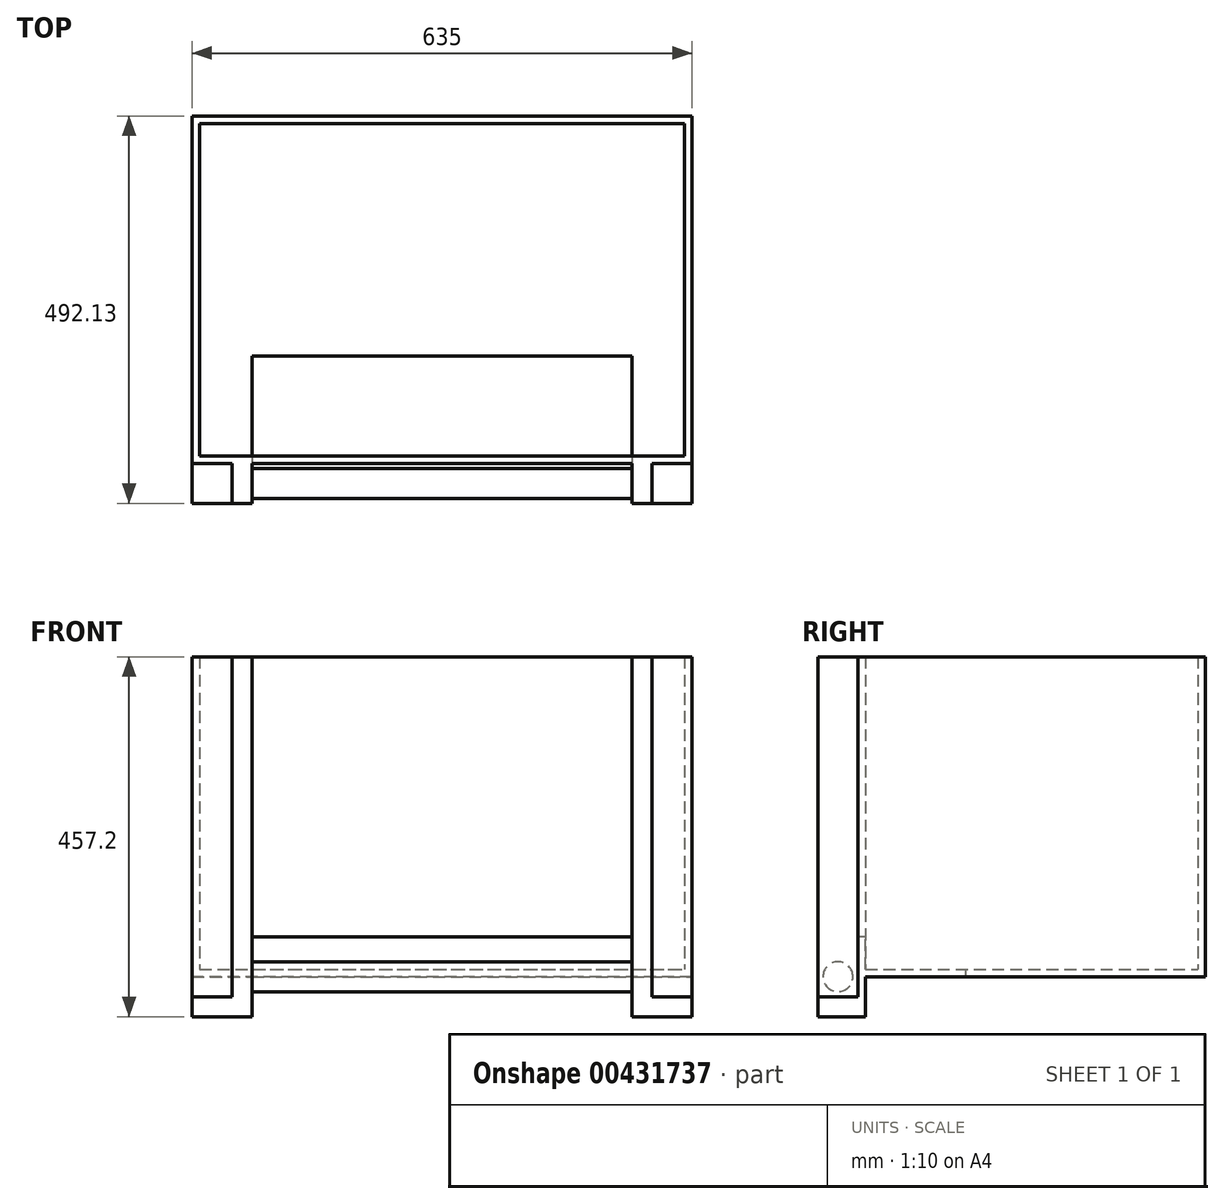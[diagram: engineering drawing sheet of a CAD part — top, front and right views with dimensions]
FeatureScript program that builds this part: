
annotation { "Feature Type Name" : "Feature", "Feature Type Description" : "" }
export const myFeature = defineFeature(function(context is Context, id is Id, definition is map)
    precondition{}
    {
        {
            var Q0;
            Q0=qCreatedBy(makeId("Top.planeOp"),FACE);
            var sketch = newSketch(context, id + "F0", { "sketchPlane" : qUnion([Q0])});
            skLineSegment(sketch, "E0", {"start": v(0, 0) * mm, "end": v(-241.3, 0) * mm, "construction": true});
            skLineSegment(sketch, "E1", {"start": v(-241.3, 0) * mm, "end": v(-241.3, 25.4) * mm, "construction": true});
            skLineSegment(sketch, "E2.bottom", {"start": v(-241.3, 25.4) * mm, "end": v(-266.7, 25.4) * mm});
            skLineSegment(sketch, "E2.top", {"start": v(-241.3, -25.4) * mm, "end": v(-266.7, -25.4) * mm});
            skLineSegment(sketch, "E2.left", {"start": v(-241.3, 25.4) * mm, "end": v(-241.3, -25.4) * mm});
            skLineSegment(sketch, "E2.right", {"start": v(-266.7, 25.4) * mm, "end": v(-266.7, -25.4) * mm});
            skSolve(sketch);
        }
        {
            var Q0;
            Q0=makeQuery(id+"F0.imprint","IMPRINT",FACE,{"disambiguationData":[TD([[makeQuery(id+"F0.imprint","IMPRINT",EDGE,{"derivedFrom":sQuery(id+"F0.wireOp",EDGE,"E2.bottom")}),1.0]])]});
            var Q1;
            Q1=makeQuery(id+"F0.imprint","IMPRINT",FACE,{"disambiguationData":[TD([[makeQuery(id+"F0.imprint","IMPRINT",EDGE,{"derivedFrom":sQuery(id+"F0.wireOp",EDGE,"9ac1ece2-4fc4-431e-a1f0-98b5578401bd1.MirrorCS")}),-1.0]])]});
            extrude(context, id + "F1", {"entities" : qUnion([Q0, Q1]), "depth" : 457.2 * mm});
        }
        {
            var Q0;
            Q0=makeQuery(id+"F1.opExtrude","SWEPT_FACE",FACE,{"disambiguationData":[OSD([sQuery(id+"F0.wireOp",EDGE,"E2.right")])]});
            var sketch = newSketch(context, id + "F2", { "sketchPlane" : qUnion([Q0])});
            skLineSegment(sketch, "E3.bottom", {"start": v(-25.4, 0) * mm, "end": v(25.4, 0) * mm});
            skLineSegment(sketch, "E3.top", {"start": v(-25.4, 25.4) * mm, "end": v(25.4, 25.4) * mm});
            skLineSegment(sketch, "E3.left", {"start": v(-25.4, 0) * mm, "end": v(-25.4, 25.4) * mm});
            skLineSegment(sketch, "E3.right", {"start": v(25.4, 0) * mm, "end": v(25.4, 25.4) * mm});
            skSolve(sketch);
        }
        {
            var Q0;
            Q0=makeQuery(id+"F2.imprint","IMPRINT",FACE,{"disambiguationData":[TD([[makeQuery(id+"F2.imprint","IMPRINT",EDGE,{"derivedFrom":sQuery(id+"F2.wireOp",EDGE,"E3.bottom")}),1.0]])]});
            extrude(context, id + "F3", {"entities" : qUnion([Q0]), "operationType" : NewBodyOperationType.ADD, "depth" : 50.8 * mm});
        }
        {
            var Q0;
            Q0=makeQuery(id+"F1.opExtrude","SWEPT_FACE",FACE,{"disambiguationData":[OSD([sQuery(id+"F0.wireOp",EDGE,"E2.left")])]});
            var sketch = newSketch(context, id + "F4", { "sketchPlane" : qUnion([Q0])});
            skLineSegment(sketch, "E4", {"start": v(0, 0) * mm, "end": v(0, 50.8) * mm, "construction": true});
            skCircle(sketch, "E5", {"center": v(0, 50.8) * mm, "radius": 19.05 * mm});
            skSolve(sketch);
        }
        {
            var Q0;
            Q0 = qSketchRegion(id + "F4", true);
            extrude(context, id + "F5", {"entities" : qUnion([Q0]), "operationType" : NewBodyOperationType.ADD, "depth" : 241.3 * mm});
        }
        {
            var Q0;
            Q0=makeQuery(id+"F1.opExtrude","SWEPT_BODY",BODY,{"disambiguationData":[OSD([sQuery(id+"F0.wireOp",EDGE,"E2.bottom"),sQuery(id+"F0.wireOp",EDGE,"E2.top"),sQuery(id+"F0.wireOp",EDGE,"E2.right"),sQuery(id+"F0.wireOp",EDGE,"E2.left")])]});
            var Q1;
            Q1=qCreatedBy(makeId("Right.planeOp"),FACE);
            mirror(context, id + "F6", {"operationType" : NewBodyOperationType.ADD, "entities" : qUnion([Q0]), "mirrorPlane" : qUnion([Q1])});
        }
        {
            var Q0;
            Q0=makeQuery(id+"F3.boolean.opBoolean","MERGE",FACE,{"derivedFrom":[makeQuery(id+"F1.opExtrude","SWEPT_FACE",FACE,{"disambiguationData":[OSD([sQuery(id+"F0.wireOp",EDGE,"E2.bottom")])]}),makeQuery(id+"F3.opExtrude","SWEPT_FACE",FACE,{"disambiguationData":[OSD([sQuery(id+"F2.wireOp",EDGE,"E3.left")])]})]});
            var sketch = newSketch(context, id + "F7", { "sketchPlane" : qUnion([Q0])});
            skLineSegment(sketch, "E6.bottom", {"start": v(317.5, 0) * mm, "end": v(241.3, 0) * mm});
            skLineSegment(sketch, "E6.top", {"start": v(317.5, 457.2) * mm, "end": v(241.3, 457.2) * mm});
            skLineSegment(sketch, "E6.left", {"start": v(317.5, 0) * mm, "end": v(317.5, 457.2) * mm});
            skLineSegment(sketch, "E6.right", {"start": v(241.3, 0) * mm, "end": v(241.3, 457.2) * mm});
            skLineSegment(sketch, "E7.bottom", {"start": v(241.3, 457.2) * mm, "end": v(0, 457.2) * mm});
            skLineSegment(sketch, "E7.top", {"start": v(241.3, 101.6) * mm, "end": v(0, 101.6) * mm});
            skLineSegment(sketch, "E7.left", {"start": v(241.3, 457.2) * mm, "end": v(241.3, 101.6) * mm});
            skLineSegment(sketch, "E7.right", {"start": v(0, 457.2) * mm, "end": v(0, 101.6) * mm, "construction": true});
            skLineSegment(sketch, "E8.MirrorCS", {"start": v(-241.3, 0) * mm, "end": v(-241.3, 457.2) * mm});
            skLineSegment(sketch, "E9.MirrorCS", {"start": v(-241.3, 457.2) * mm, "end": v(-241.3, 101.6) * mm});
            skLineSegment(sketch, "E10.MirrorCS", {"start": v(-317.5, 0) * mm, "end": v(-241.3, 0) * mm});
            skLineSegment(sketch, "E11.MirrorCS", {"start": v(-317.5, 457.2) * mm, "end": v(-241.3, 457.2) * mm});
            skLineSegment(sketch, "E12.MirrorCS", {"start": v(-241.3, 101.6) * mm, "end": v(0, 101.6) * mm});
            skLineSegment(sketch, "E13.MirrorCS", {"start": v(-241.3, 457.2) * mm, "end": v(0, 457.2) * mm});
            skLineSegment(sketch, "E14.MirrorCS", {"start": v(-317.5, 0) * mm, "end": v(-317.5, 457.2) * mm});
            skSolve(sketch);
        }
        {
            var Q0;
            Q0=makeQuery(id+"F7.imprint","IMPRINT",FACE,{"disambiguationData":[TD([[makeQuery(id+"F7.imprint","IMPRINT",EDGE,{"derivedFrom":sQuery(id+"F7.wireOp",EDGE,"E8.MirrorCS")}),1.0]])]});
            var Q1;
            {var subQ1=sQuery(id+"F0.wireOp",EDGE,"E2.right");var subQ2=sQuery(id+"F0.wireOp",EDGE,"E2.bottom");var subQ3=makeQuery(id+"F1.opExtrude","SWEPT_EDGE",EDGE,{"disambiguationData":[OSD([subQ2,subQ1])]});Q1=makeQuery(id+"F7.imprint","IMPRINT",FACE,{"disambiguationData":[TD([[makeQuery(id+"F7.imprint","IMPRINT",EDGE,{"derivedFrom":subQ3}),1.0]])]});}
            var Q2;
            {var subQ1=sQuery(id+"F7.wireOp",EDGE,"E6.bottom");Q2=makeQuery(id+"F7.imprint","IMPRINT",FACE,{"disambiguationData":[TD([[makeQuery(id+"F7.imprint","IMPRINT",EDGE,{"derivedFrom":subQ1}),1.0]])]});}
            var Q3;
            Q3=makeQuery(id+"F7.imprint","IMPRINT",FACE,{"disambiguationData":[TD([[makeQuery(id+"F7.imprint","IMPRINT",EDGE,{"derivedFrom":sQuery(id+"F7.wireOp",EDGE,"E7.bottom")}),1.0]])]});
            extrude(context, id + "F8", {"entities" : qUnion([Q0, Q1, Q2, Q3]), "operationType" : NewBodyOperationType.ADD, "depth" : 9.52 * mm});
        }
        {
            var Q0;
            Q0=qCreatedBy(makeId("Top.planeOp"),FACE);
            cPlane(context, id + "F9", {"entities" : qUnion([Q0]), "cplaneType" : CPlaneType.OFFSET, "offset" : 50.8 * mm, "width" : 152.4 * mm, "height" : 152.4 * mm});
        }
        {
            var Q0;
            Q0=qCreatedBy(id+"F9.planeOp",FACE);
            var sketch = newSketch(context, id + "F10", { "sketchPlane" : qUnion([Q0])});
            skLineSegment(sketch, "E15", {"start": v(0, 0) * mm, "end": v(0, 34.93) * mm});
            skLineSegment(sketch, "E16", {"start": v(0, 34.93) * mm, "end": v(-241.3, 34.93) * mm});
            skLineSegment(sketch, "E17", {"start": v(-241.3, 34.93) * mm, "end": v(-241.3, 161.92) * mm});
            skLineSegment(sketch, "E18", {"start": v(-241.3, 161.92) * mm, "end": v(241.3, 161.92) * mm});
            skLineSegment(sketch, "E19", {"start": v(241.3, 161.92) * mm, "end": v(241.3, 34.93) * mm});
            skLineSegment(sketch, "E20", {"start": v(241.3, 34.93) * mm, "end": v(307.98, 34.93) * mm});
            skLineSegment(sketch, "E21", {"start": v(307.98, 34.93) * mm, "end": v(307.98, 466.73) * mm});
            skLineSegment(sketch, "E22", {"start": v(307.98, 466.73) * mm, "end": v(-307.98, 466.73) * mm});
            skLineSegment(sketch, "E23", {"start": v(-307.98, 466.73) * mm, "end": v(-307.98, 34.93) * mm});
            skLineSegment(sketch, "E24", {"start": v(-307.98, 34.93) * mm, "end": v(-241.3, 34.93) * mm});
            skSolve(sketch);
        }
        {
            var Q0;
            Q0=makeQuery(id+"F10.imprint","IMPRINT",FACE,{"disambiguationData":[TD([[makeQuery(id+"F10.imprint","IMPRINT",EDGE,{"derivedFrom":sQuery(id+"F10.wireOp",EDGE,"E17")}),1.0]])]});
            extrude(context, id + "F11", {"entities" : qUnion([Q0]), "operationType" : NewBodyOperationType.ADD, "depth" : 9.52 * mm});
        }
        {
            var Q0;
            Q0=makeQuery(id+"F8.opExtrude","CAP_FACE",FACE,{"disambiguationData":[OSD([sQuery(id+"F7.wireOp",EDGE,"E6.bottom"),sQuery(id+"F7.wireOp",EDGE,"E6.top"),sQuery(id+"F7.wireOp",EDGE,"E6.left"),sQuery(id+"F7.wireOp",EDGE,"E6.right"),sQuery(id+"F7.wireOp",EDGE,"E7.bottom"),sQuery(id+"F7.wireOp",EDGE,"E7.top"),sQuery(id+"F7.wireOp",EDGE,"E8.MirrorCS"),sQuery(id+"F7.wireOp",EDGE,"E10.MirrorCS"),sQuery(id+"F7.wireOp",EDGE,"E11.MirrorCS"),sQuery(id+"F7.wireOp",EDGE,"E12.MirrorCS"),sQuery(id+"F7.wireOp",EDGE,"E13.MirrorCS"),sQuery(id+"F7.wireOp",EDGE,"E14.MirrorCS")])],"isStart":false});
            var sketch = newSketch(context, id + "F12", { "sketchPlane" : qUnion([Q0])});
            skLineSegment(sketch, "E25.bottom", {"start": v(-317.5, 457.2) * mm, "end": v(-307.98, 457.2) * mm});
            skLineSegment(sketch, "E25.top", {"start": v(-317.5, 50.8) * mm, "end": v(-307.98, 50.8) * mm});
            skLineSegment(sketch, "E25.left", {"start": v(-317.5, 457.2) * mm, "end": v(-317.5, 50.8) * mm});
            skLineSegment(sketch, "E25.right", {"start": v(-307.98, 457.2) * mm, "end": v(-307.98, 50.8) * mm});
            skLineSegment(sketch, "E26.bottom", {"start": v(307.98, 50.8) * mm, "end": v(317.5, 50.8) * mm});
            skLineSegment(sketch, "E26.top", {"start": v(307.98, 457.2) * mm, "end": v(317.5, 457.2) * mm});
            skLineSegment(sketch, "E26.left", {"start": v(307.98, 50.8) * mm, "end": v(307.98, 457.2) * mm});
            skLineSegment(sketch, "E26.right", {"start": v(317.5, 50.8) * mm, "end": v(317.5, 457.2) * mm});
            skSolve(sketch);
        }
        {
            var Q0;
            Q0 = qSketchRegion(id + "F12", true);
            extrude(context, id + "F13", {"entities" : qUnion([Q0]), "operationType" : NewBodyOperationType.ADD, "depth" : 431.8 * mm});
        }
        {
            var Q0;
            Q0=makeQuery(id+"F11.opExtrude","CAP_FACE",FACE,{"disambiguationData":[OSD([sQuery(id+"F10.wireOp",EDGE,"E17"),sQuery(id+"F10.wireOp",EDGE,"E18"),sQuery(id+"F10.wireOp",EDGE,"E19"),sQuery(id+"F10.wireOp",EDGE,"E20"),sQuery(id+"F10.wireOp",EDGE,"E21"),sQuery(id+"F10.wireOp",EDGE,"E22"),sQuery(id+"F10.wireOp",EDGE,"E23"),sQuery(id+"F10.wireOp",EDGE,"E24")])],"isStart":false});
            var sketch = newSketch(context, id + "F14", { "sketchPlane" : qUnion([Q0])});
            skLineSegment(sketch, "E27.bottom", {"start": v(-307.98, 466.73) * mm, "end": v(307.98, 466.73) * mm});
            skLineSegment(sketch, "E27.top", {"start": v(-307.98, 457.2) * mm, "end": v(307.98, 457.2) * mm});
            skLineSegment(sketch, "E27.left", {"start": v(-307.98, 466.73) * mm, "end": v(-307.98, 457.2) * mm});
            skLineSegment(sketch, "E27.right", {"start": v(307.98, 466.73) * mm, "end": v(307.98, 457.2) * mm});
            skSolve(sketch);
        }
        {
            var Q0;
            Q0=makeQuery(id+"F14.imprint","IMPRINT",FACE,{"disambiguationData":[TD([[makeQuery(id+"F14.imprint","IMPRINT",EDGE,{"derivedFrom":sQuery(id+"F14.wireOp",EDGE,"E27.bottom")}),1.0]])]});
            var Q1;
            {var subQ0=makeQuery(id+"F1.opExtrude","CAP_FACE",FACE,{"disambiguationData":[OSD([sQuery(id+"F0.wireOp",EDGE,"E2.bottom"),sQuery(id+"F0.wireOp",EDGE,"E2.top"),sQuery(id+"F0.wireOp",EDGE,"E2.right"),sQuery(id+"F0.wireOp",EDGE,"E2.left")])],"isStart":false});Q1=makeQuery(id+"F13.boolean.opBoolean","MERGE",FACE,{"derivedFrom":[makeQuery(id+"F8.boolean.opBoolean","MERGE",FACE,{"derivedFrom":[subQ0,makeQuery(id+"F6.opPattern","COPY",FACE,{"derivedFrom":subQ0,"instanceName":"1"}),makeQuery(id+"F8.opExtrude","SWEPT_FACE",FACE,{"disambiguationData":[OSD([sQuery(id+"F7.wireOp",EDGE,"E6.top"),sQuery(id+"F7.wireOp",EDGE,"E7.bottom"),sQuery(id+"F7.wireOp",EDGE,"E11.MirrorCS"),sQuery(id+"F7.wireOp",EDGE,"E13.MirrorCS")])]})]}),makeQuery(id+"F13.opExtrude","SWEPT_FACE",FACE,{"disambiguationData":[OSD([sQuery(id+"F12.wireOp",EDGE,"E25.bottom")])]}),makeQuery(id+"F13.opExtrude","SWEPT_FACE",FACE,{"disambiguationData":[OSD([sQuery(id+"F12.wireOp",EDGE,"E26.top")])]})]});}
            extrude(context, id + "F15", {"entities" : qUnion([Q0]), "operationType" : NewBodyOperationType.ADD, "endBound" : BoundingType.UP_TO_SURFACE, "endBoundEntityFace" : qUnion([Q1]), "depth" : 25.4 * mm});
        }
    });
